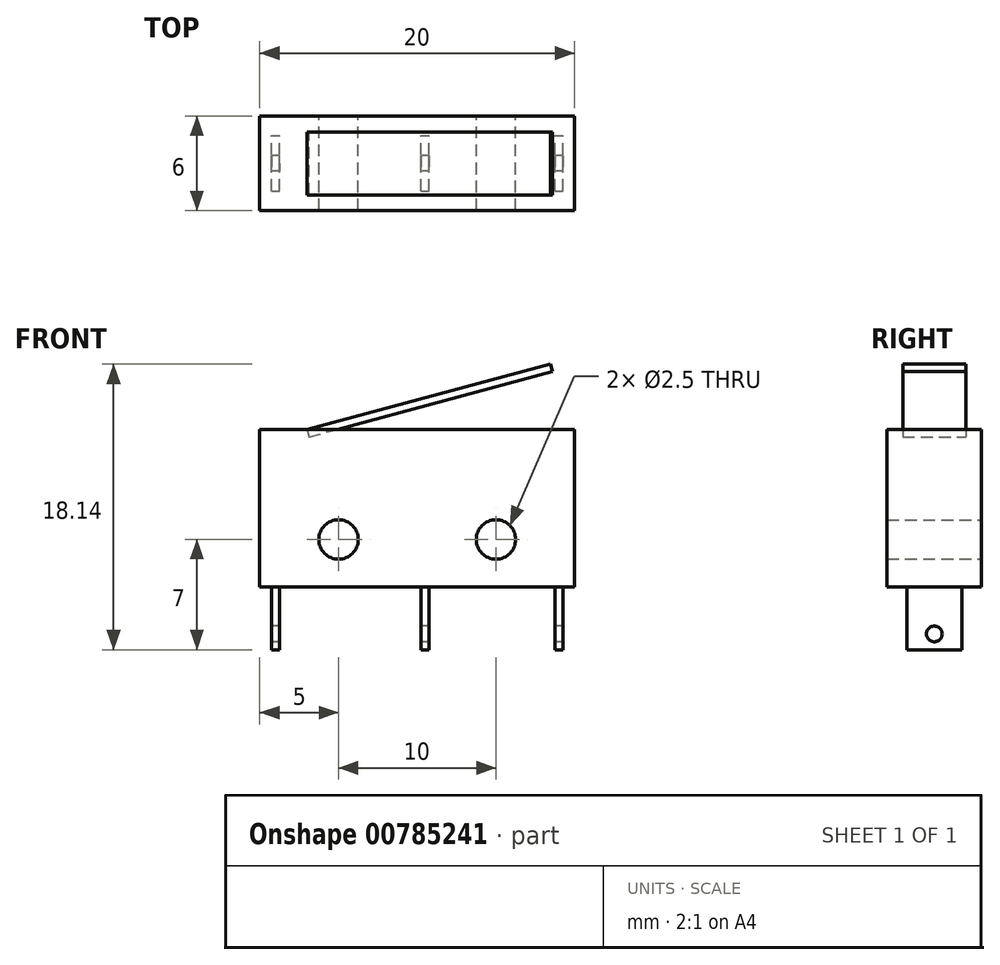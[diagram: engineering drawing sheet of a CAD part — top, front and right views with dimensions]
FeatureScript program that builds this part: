
annotation { "Feature Type Name" : "Feature", "Feature Type Description" : "" }
export const myFeature = defineFeature(function(context is Context, id is Id, definition is map)
    precondition{}
    {
        {
            var Q0;
            Q0=qCreatedBy(makeId("Front.planeOp"),FACE);
            var sketch = newSketch(context, id + "F0", { "sketchPlane" : qUnion([Q0])});
            skLineSegment(sketch, "E0.bottom", {"start": v(-10, 0) * mm, "end": v(10, 0) * mm});
            skLineSegment(sketch, "E0.top", {"start": v(-10, 10) * mm, "end": v(10, 10) * mm});
            skLineSegment(sketch, "E0.left", {"start": v(-10, 0) * mm, "end": v(-10, 10) * mm});
            skLineSegment(sketch, "E0.right", {"start": v(10, 0) * mm, "end": v(10, 10) * mm});
            skPoint(sketch, "E0.middle", {"position": v(0, 5) * mm});
            skCircle(sketch, "E1", {"center": v(-5, 3) * mm, "radius": 1.25 * mm});
            skCircle(sketch, "E2.MirrorC", {"center": v(5, 3) * mm, "radius": 1.25 * mm});
            skSolve(sketch);
        }
        {
            var Q0;
            Q0=makeQuery(id+"F0.imprint","IMPRINT",FACE,{"disambiguationData":[TD([[makeQuery(id+"F0.imprint","IMPRINT",EDGE,{"derivedFrom":sQuery(id+"F0.wireOp",EDGE,"E0.bottom")}),1.0]])]});
            extrude(context, id + "F1", {"entities" : qUnion([Q0]), "endBound" : BoundingType.SYMMETRIC, "depth" : 6 * mm, "offsetDistance" : 25 * mm});
        }
        {
            var Q0;
            Q0=qCreatedBy(makeId("Front.planeOp"),FACE);
            var sketch = newSketch(context, id + "F2", { "sketchPlane" : qUnion([Q0])});
            skLineSegment(sketch, "E3", {"start": v(-7, 10) * mm, "end": v(-6.87, 9.52) * mm});
            skLineSegment(sketch, "E4", {"start": v(-6.87, 9.52) * mm, "end": v(8.58, 13.66) * mm});
            skLineSegment(sketch, "E5", {"start": v(8.58, 13.66) * mm, "end": v(8.45, 14.14) * mm});
            skLineSegment(sketch, "E6", {"start": v(8.45, 14.14) * mm, "end": v(-7, 10) * mm});
            skSolve(sketch);
        }
        {
            var Q0;
            Q0=makeQuery(id+"F2.imprint","IMPRINT",FACE,{"disambiguationData":[TD([[makeQuery(id+"F2.imprint","IMPRINT",EDGE,{"derivedFrom":sQuery(id+"F2.wireOp",EDGE,"E3")}),1.0]])]});
            extrude(context, id + "F3", {"entities" : qUnion([Q0]), "endBound" : BoundingType.SYMMETRIC, "depth" : 4 * mm, "offsetDistance" : 25 * mm});
        }
        {
            var Q0;
            Q0=qCreatedBy(makeId("Front.planeOp"),FACE);
            var sketch = newSketch(context, id + "F4", { "sketchPlane" : qUnion([Q0])});
            skLineSegment(sketch, "E7.bottom", {"start": v(-9.25, 0) * mm, "end": v(-8.75, 0) * mm});
            skLineSegment(sketch, "E7.top", {"start": v(-9.25, -4) * mm, "end": v(-8.75, -4) * mm});
            skLineSegment(sketch, "E7.left", {"start": v(-9.25, 0) * mm, "end": v(-9.25, -4) * mm});
            skLineSegment(sketch, "E7.right", {"start": v(-8.75, 0) * mm, "end": v(-8.75, -4) * mm});
            skLineSegment(sketch, "E8.bottom", {"start": v(8.75, 0) * mm, "end": v(9.25, 0) * mm});
            skLineSegment(sketch, "E8.top", {"start": v(8.75, -4) * mm, "end": v(9.25, -4) * mm});
            skLineSegment(sketch, "E8.left", {"start": v(8.75, 0) * mm, "end": v(8.75, -4) * mm});
            skLineSegment(sketch, "E8.right", {"start": v(9.25, 0) * mm, "end": v(9.25, -4) * mm});
            skLineSegment(sketch, "E9.bottom", {"start": v(0.25, 0) * mm, "end": v(0.75, 0) * mm});
            skLineSegment(sketch, "E9.top", {"start": v(0.25, -4) * mm, "end": v(0.75, -4) * mm});
            skLineSegment(sketch, "E9.left", {"start": v(0.25, 0) * mm, "end": v(0.25, -4) * mm});
            skLineSegment(sketch, "E9.right", {"start": v(0.75, 0) * mm, "end": v(0.75, -4) * mm});
            skSolve(sketch);
        }
        {
            var Q0;
            Q0=makeQuery(id+"F4.imprint","IMPRINT",FACE,{"disambiguationData":[TD([[makeQuery(id+"F4.imprint","IMPRINT",EDGE,{"derivedFrom":sQuery(id+"F4.wireOp",EDGE,"E7.bottom")}),-1.0]])]});
            var Q1;
            Q1=makeQuery(id+"F4.imprint","IMPRINT",FACE,{"disambiguationData":[TD([[makeQuery(id+"F4.imprint","IMPRINT",EDGE,{"derivedFrom":sQuery(id+"F4.wireOp",EDGE,"E9.bottom")}),-1.0]])]});
            var Q2;
            Q2=makeQuery(id+"F4.imprint","IMPRINT",FACE,{"disambiguationData":[TD([[makeQuery(id+"F4.imprint","IMPRINT",EDGE,{"derivedFrom":sQuery(id+"F4.wireOp",EDGE,"E8.bottom")}),-1.0]])]});
            extrude(context, id + "F5", {"entities" : qUnion([Q0, Q1, Q2]), "endBound" : BoundingType.SYMMETRIC, "depth" : 3.5 * mm, "offsetDistance" : 25 * mm});
        }
        {
            var Q0;
            Q0=makeQuery(id+"F5.opExtrude","SWEPT_FACE",FACE,{"disambiguationData":[OSD([sQuery(id+"F4.wireOp",EDGE,"E7.left")])]});
            var sketch = newSketch(context, id + "F6", { "sketchPlane" : qUnion([Q0])});
            skCircle(sketch, "E10", {"center": v(0, -3) * mm, "radius": 0.5 * mm});
            skSolve(sketch);
        }
        {
            var Q0;
            Q0=makeQuery(id+"F6.imprint","IMPRINT",FACE,{"disambiguationData":[TD([[makeQuery(id+"F6.imprint","IMPRINT",EDGE,{"derivedFrom":sQuery(id+"F6.wireOp",EDGE,"E10")}),1.0]])]});
            extrude(context, id + "F7", {"entities" : qUnion([Q0]), "operationType" : NewBodyOperationType.REMOVE, "endBound" : BoundingType.THROUGH_ALL, "oppositeDirection" : true, "depth" : 25 * mm, "offsetDistance" : 25 * mm});
        }
    });
